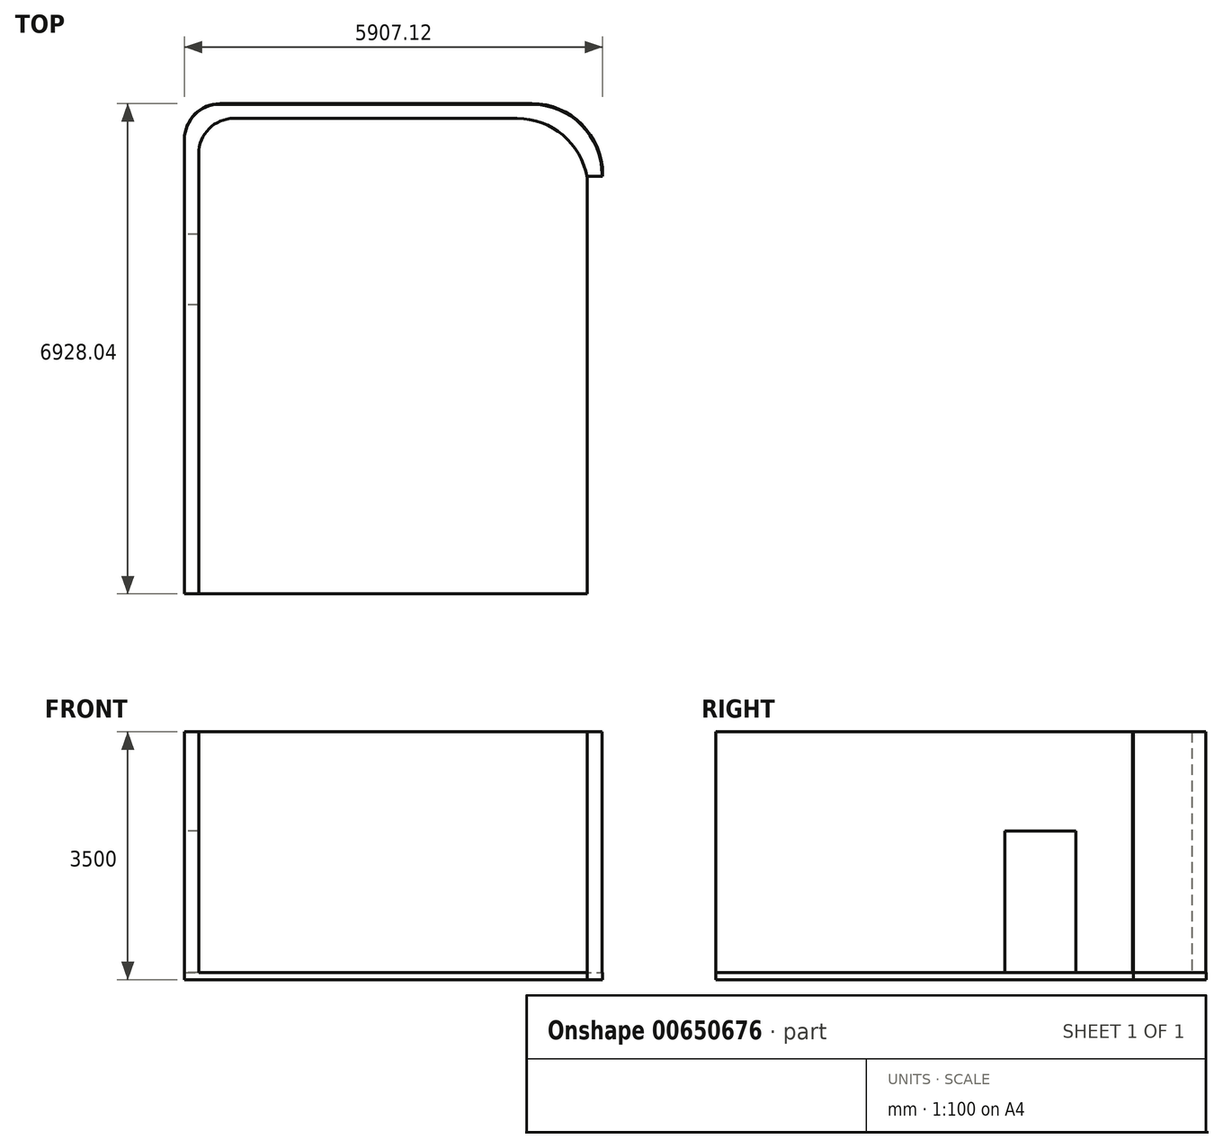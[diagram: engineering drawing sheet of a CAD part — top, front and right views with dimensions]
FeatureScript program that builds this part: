
annotation { "Feature Type Name" : "Feature", "Feature Type Description" : "" }
export const myFeature = defineFeature(function(context is Context, id is Id, definition is map)
    precondition{}
    {
        {
            var Q0;
            Q0=qCreatedBy(makeId("Top.planeOp"),FACE);
            var sketch = newSketch(context, id + "F0", { "sketchPlane" : qUnion([Q0])});
            skLineSegment(sketch, "E0.bottom", {"start": v(-2945.17, 4137.07) * mm, "end": v(1454.83, 4137.07) * mm});
            skLineSegment(sketch, "E0.top", {"start": v(-3445.17, -3012.93) * mm, "end": v(2454.83, -3012.93) * mm});
            skLineSegment(sketch, "E0.left", {"start": v(-3445.17, 3637.07) * mm, "end": v(-3445.17, -3012.93) * mm});
            skLineSegment(sketch, "E0.right", {"start": v(2454.83, 3137.07) * mm, "end": v(2454.83, -3012.93) * mm});
            skLineSegment(sketch, "E1.bottom", {"start": v(-2745.17, 3937.07) * mm, "end": v(1254.83, 3937.07) * mm});
            skLineSegment(sketch, "E1.top", {"start": v(-3245.17, -2812.93) * mm, "end": v(2254.83, -2812.93) * mm});
            skLineSegment(sketch, "E1.left", {"start": v(-3245.17, 3437.07) * mm, "end": v(-3245.17, -2812.93) * mm});
            skLineSegment(sketch, "E1.right", {"start": v(2254.83, 2937.07) * mm, "end": v(2254.83, -2812.93) * mm});
            skPoint(sketch, "E2.visualSharp", {"position": v(-3445.17, 4137.07) * mm});
            skArc(sketch, "E2.filletArc", {"start": v(-2945.17, 4137.07) * mm, "mid": v(-3298.73, 3990.63) * mm, "end": v(-3445.17, 3637.07) * mm});
            skPoint(sketch, "E3.visualSharp", {"position": v(-3245.17, 3937.07) * mm});
            skArc(sketch, "E3.filletArc", {"start": v(-2745.17, 3937.07) * mm, "mid": v(-3098.73, 3790.63) * mm, "end": v(-3245.17, 3437.07) * mm});
            skPoint(sketch, "E4.visualSharp", {"position": v(2454.83, 4137.07) * mm});
            skArc(sketch, "E4.filletArc", {"start": v(2454.83, 3137.07) * mm, "mid": v(2161.93, 3844.18) * mm, "end": v(1454.83, 4137.07) * mm});
            skPoint(sketch, "E5.visualSharp", {"position": v(2254.83, 3937.07) * mm});
            skArc(sketch, "E5.filletArc", {"start": v(2254.83, 2937.07) * mm, "mid": v(1961.93, 3644.18) * mm, "end": v(1254.83, 3937.07) * mm});
            skSolve(sketch);
        }
        {
            var Q0;
            Q0=makeQuery(id+"F0.imprint","IMPRINT",FACE,{"disambiguationData":[TD([[makeQuery(id+"F0.imprint","IMPRINT",EDGE,{"derivedFrom":sQuery(id+"F0.wireOp",EDGE,"E0.bottom")}),-1.0]])]});
            extrude(context, id + "F1", {"entities" : qUnion([Q0]), "depth" : 3500 * mm, "offsetDistance" : 25 * mm});
        }
        {
            var Q0;
            Q0=makeQuery(id+"F1.opExtrude","CAP_FACE",FACE,{"disambiguationData":[OSD([sQuery(id+"F0.wireOp",EDGE,"E0.bottom"),sQuery(id+"F0.wireOp",EDGE,"E0.top"),sQuery(id+"F0.wireOp",EDGE,"E0.left"),sQuery(id+"F0.wireOp",EDGE,"E0.right"),sQuery(id+"F0.wireOp",EDGE,"E1.bottom"),sQuery(id+"F0.wireOp",EDGE,"E1.top"),sQuery(id+"F0.wireOp",EDGE,"E1.left"),sQuery(id+"F0.wireOp",EDGE,"E1.right"),sQuery(id+"F0.wireOp",EDGE,"E2.filletArc"),sQuery(id+"F0.wireOp",EDGE,"E3.filletArc"),sQuery(id+"F0.wireOp",EDGE,"E4.filletArc"),sQuery(id+"F0.wireOp",EDGE,"E5.filletArc")])],"isStart":true});
            var sketch = newSketch(context, id + "F2", { "sketchPlane" : qUnion([Q0])});
            skLineSegment(sketch, "E6.bottom", {"start": v(-3445.17, 3012.93) * mm, "end": v(2461.95, 3012.93) * mm});
            skLineSegment(sketch, "E6.top", {"start": v(-2945.17, -4144.82) * mm, "end": v(1461.95, -4144.82) * mm});
            skLineSegment(sketch, "E6.left", {"start": v(-3445.17, 3012.93) * mm, "end": v(-3445.17, -3644.82) * mm});
            skLineSegment(sketch, "E6.right", {"start": v(2461.95, 3012.93) * mm, "end": v(2461.95, -3144.82) * mm});
            skPoint(sketch, "E7.visualSharp", {"position": v(2461.95, -4144.82) * mm});
            skArc(sketch, "E7.filletArc", {"start": v(1461.95, -4144.82) * mm, "mid": v(2169.05, -3851.92) * mm, "end": v(2461.95, -3144.82) * mm});
            skPoint(sketch, "E8.visualSharp", {"position": v(-3445.17, -4144.82) * mm});
            skArc(sketch, "E8.filletArc", {"start": v(-3445.17, -3644.82) * mm, "mid": v(-3298.73, -3998.37) * mm, "end": v(-2945.17, -4144.82) * mm});
            skSolve(sketch);
        }
        {
            var Q0;
            Q0 = qSketchRegion(id + "F2", true);
            extrude(context, id + "F3", {"entities" : qUnion([Q0]), "operationType" : NewBodyOperationType.ADD, "oppositeDirection" : true, "depth" : 100 * mm, "offsetDistance" : 25 * mm});
        }
        {
            var Q0;
            Q0=makeQuery(id+"F3.boolean.opBoolean","MERGE",FACE,{"derivedFrom":[makeQuery(id+"F1.opExtrude","SWEPT_FACE",FACE,{"disambiguationData":[OSD([sQuery(id+"F0.wireOp",EDGE,"E0.left")])]}),makeQuery(id+"F3.opExtrude","SWEPT_FACE",FACE,{"disambiguationData":[OSD([sQuery(id+"F2.wireOp",EDGE,"E6.left")])]})]});
            var sketch = newSketch(context, id + "F4", { "sketchPlane" : qUnion([Q0])});
            skLineSegment(sketch, "E9.bottom", {"start": v(-2300.58, 100) * mm, "end": v(-1300.58, 100) * mm});
            skLineSegment(sketch, "E9.top", {"start": v(-2300.58, 2100) * mm, "end": v(-1300.58, 2100) * mm});
            skLineSegment(sketch, "E9.left", {"start": v(-2300.58, 100) * mm, "end": v(-2300.58, 2100) * mm});
            skLineSegment(sketch, "E9.right", {"start": v(-1300.58, 100) * mm, "end": v(-1300.58, 2100) * mm});
            skSolve(sketch);
        }
        {
            var Q0;
            Q0 = qSketchRegion(id + "F4", true);
            extrude(context, id + "F5", {"entities" : qUnion([Q0]), "operationType" : NewBodyOperationType.REMOVE, "oppositeDirection" : true, "depth" : 560 * mm, "offsetDistance" : 25 * mm});
        }
        {
            var Q0;
            Q0=makeQuery(id+"F1.opExtrude","CAP_FACE",FACE,{"disambiguationData":[OSD([sQuery(id+"F0.wireOp",EDGE,"E0.bottom"),sQuery(id+"F0.wireOp",EDGE,"E0.top"),sQuery(id+"F0.wireOp",EDGE,"E0.left"),sQuery(id+"F0.wireOp",EDGE,"E0.right"),sQuery(id+"F0.wireOp",EDGE,"E1.bottom"),sQuery(id+"F0.wireOp",EDGE,"E1.top"),sQuery(id+"F0.wireOp",EDGE,"E1.left"),sQuery(id+"F0.wireOp",EDGE,"E1.right"),sQuery(id+"F0.wireOp",EDGE,"E2.filletArc"),sQuery(id+"F0.wireOp",EDGE,"E3.filletArc"),sQuery(id+"F0.wireOp",EDGE,"E4.filletArc"),sQuery(id+"F0.wireOp",EDGE,"E5.filletArc")])],"isStart":false});
            var sketch = newSketch(context, id + "F6", { "sketchPlane" : qUnion([Q0])});
            skLineSegment(sketch, "E10.bottom", {"start": v(-3555.57, -2783.22) * mm, "end": v(2658.89, -2783.22) * mm});
            skLineSegment(sketch, "E10.top", {"start": v(-3555.57, -3383.71) * mm, "end": v(2658.89, -3383.71) * mm});
            skLineSegment(sketch, "E10.left", {"start": v(-3555.57, -2783.22) * mm, "end": v(-3555.57, -3383.71) * mm});
            skLineSegment(sketch, "E10.right", {"start": v(2658.89, -2783.22) * mm, "end": v(2658.89, -3383.71) * mm});
            skLineSegment(sketch, "E11.bottom", {"start": v(2658.89, -2783.22) * mm, "end": v(2241.3, -2783.22) * mm});
            skLineSegment(sketch, "E11.top", {"start": v(2658.89, 3115.66) * mm, "end": v(2241.3, 3115.66) * mm});
            skLineSegment(sketch, "E11.left", {"start": v(2658.89, -2783.22) * mm, "end": v(2658.89, 3115.66) * mm});
            skLineSegment(sketch, "E11.right", {"start": v(2241.3, -2783.22) * mm, "end": v(2241.3, 3115.66) * mm});
            skSolve(sketch);
        }
        {
            var Q0;
            Q0 = qSketchRegion(id + "F6", true);
            extrude(context, id + "F7", {"entities" : qUnion([Q0]), "operationType" : NewBodyOperationType.REMOVE, "oppositeDirection" : true, "depth" : 3610 * mm, "offsetDistance" : 25 * mm});
        }
    });
